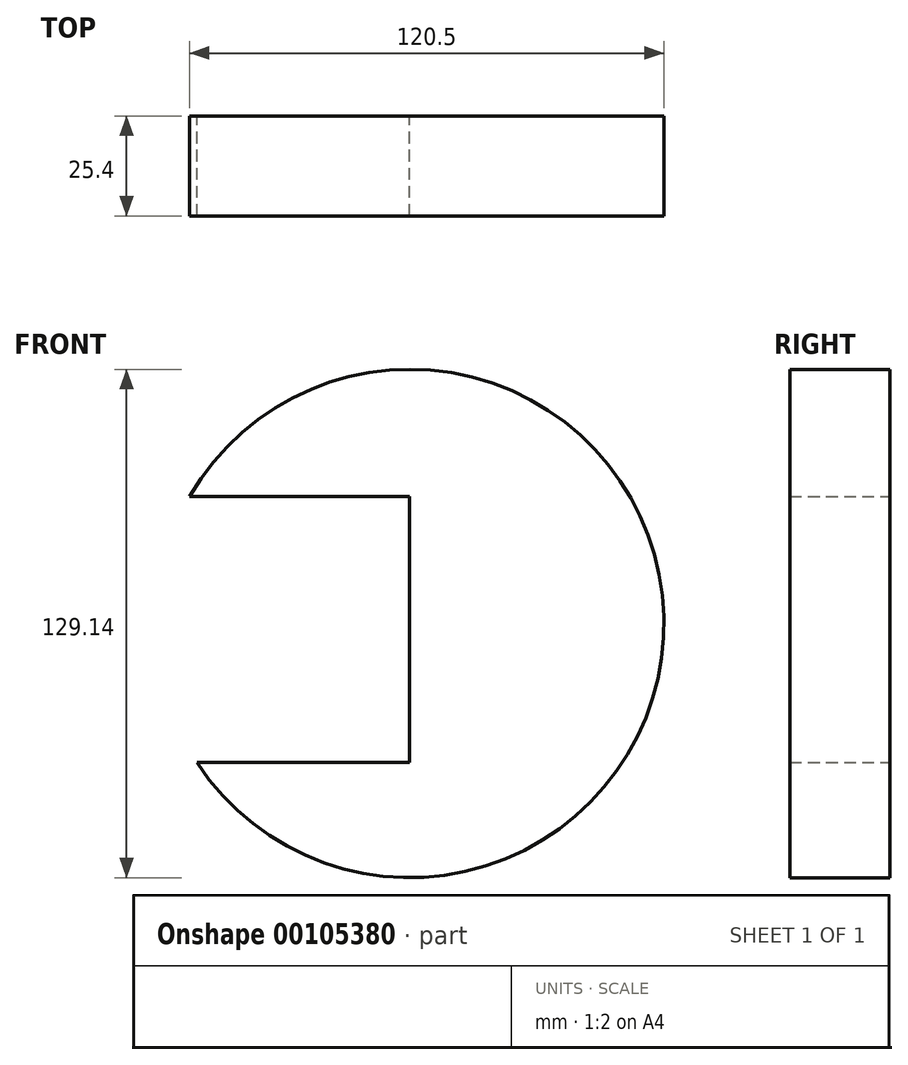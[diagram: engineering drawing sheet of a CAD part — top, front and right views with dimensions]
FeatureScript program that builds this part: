
annotation { "Feature Type Name" : "Feature", "Feature Type Description" : "" }
export const myFeature = defineFeature(function(context is Context, id is Id, definition is map)
    precondition{}
    {
        {
            var Q0;
            Q0=qCreatedBy(makeId("Front.planeOp"),FACE);
            var sketch = newSketch(context, id + "F0", { "sketchPlane" : qUnion([Q0])});
            skCircle(sketch, "E0", {"center": v(0, 0) * mm, "radius": 64.57 * mm});
            skLineSegment(sketch, "E1.bottom", {"start": v(0, -35.33) * mm, "end": v(-150.48, -35.33) * mm});
            skLineSegment(sketch, "E1.top", {"start": v(0, 32.27) * mm, "end": v(-150.48, 32.27) * mm});
            skLineSegment(sketch, "E1.left", {"start": v(0, -35.33) * mm, "end": v(0, 32.27) * mm});
            skLineSegment(sketch, "E1.right", {"start": v(-150.48, -35.33) * mm, "end": v(-150.48, 32.27) * mm});
            skSolve(sketch);
        }
        {
            var Q0;
            {var subQ5=sQuery(id+"F0.wireOp",EDGE,"E1.left");Q0=makeQuery(id+"F0.imprint","IMPRINT",FACE,{"disambiguationData":[TD([[makeQuery(id+"F0.imprint","IMPRINT",EDGE,{"derivedFrom":subQ5}),-1.0]])]});}
            extrude(context, id + "F1", {"entities" : qUnion([Q0]), "endBound" : BoundingType.SYMMETRIC, "depth" : 25.4 * mm});
        }
    });
